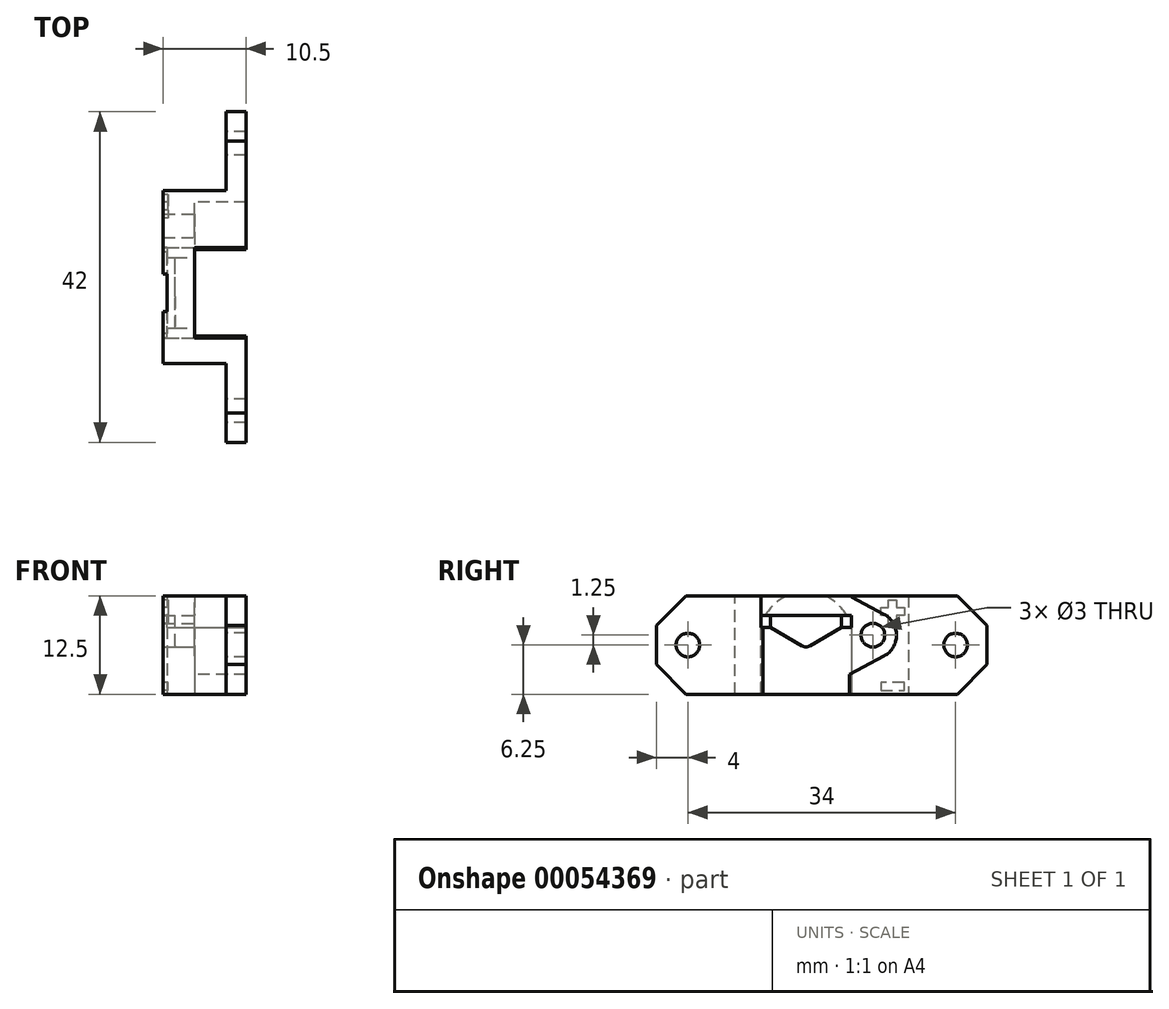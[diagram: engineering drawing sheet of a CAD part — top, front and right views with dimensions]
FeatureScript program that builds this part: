
annotation { "Feature Type Name" : "Feature", "Feature Type Description" : "" }
export const myFeature = defineFeature(function(context is Context, id is Id, definition is map)
    precondition{}
    {
        {
            var Q0;
            Q0=qCreatedBy(makeId("Right.planeOp"),FACE);
            var sketch = newSketch(context, id + "F0", { "sketchPlane" : qUnion([Q0])});
            skLineSegment(sketch, "E0", {"start": v(-5.75, 10) * mm, "end": v(-5.75, 8.5) * mm});
            skLineSegment(sketch, "E1", {"start": v(-5.75, 8.5) * mm, "end": v(-4.5, 8.5) * mm});
            skLineSegment(sketch, "E2", {"start": v(-4.5, 8.5) * mm, "end": v(-4.5, 10) * mm});
            skLineSegment(sketch, "E3", {"start": v(-4.5, 10) * mm, "end": v(-5.75, 10) * mm});
            skLineSegment(sketch, "E4.MirrorCS", {"start": v(4.5, 8.5) * mm, "end": v(4.5, 10) * mm});
            skLineSegment(sketch, "E5.MirrorCS", {"start": v(5.75, 8.5) * mm, "end": v(4.5, 8.5) * mm});
            skLineSegment(sketch, "E6.MirrorCS", {"start": v(4.5, 10) * mm, "end": v(5.75, 10) * mm});
            skLineSegment(sketch, "E7.MirrorCS", {"start": v(5.75, 10) * mm, "end": v(5.75, 8.5) * mm});
            skArc(sketch, "E8", {"start": v(-5.2, 10) * mm, "mid": v(0, 13) * mm, "end": v(5.2, 10) * mm});
            skLineSegment(sketch, "E9", {"start": v(-5.75, 8.5) * mm, "end": v(-5.75, 0) * mm});
            skLineSegment(sketch, "E10.MirrorCS", {"start": v(5.75, 8.5) * mm, "end": v(5.75, 0) * mm});
            skLineSegment(sketch, "E11", {"start": v(-5.75, 0) * mm, "end": v(5.75, 0) * mm});
            skCircle(sketch, "E12", {"center": v(0, 7) * mm, "radius": 8 * mm, "construction": true});
            skSolve(sketch);
        }
        {
            var Q0;
            Q0=qCreatedBy(makeId("Right.planeOp"),FACE);
            cPlane(context, id + "F1", {"entities" : qUnion([Q0]), "cplaneType" : CPlaneType.OFFSET, "offset" : 4 * mm, "width" : 150 * mm, "height" : 150 * mm});
        }
        {
            var Q0;
            Q0=qCreatedBy(id+"F1.planeOp",FACE);
            var sketch = newSketch(context, id + "F2", { "sketchPlane" : qUnion([Q0])});
            skLineSegment(sketch, "E13", {"start": v(-5.5, 0) * mm, "end": v(-5.5, 12.5) * mm, "construction": true});
            skLineSegment(sketch, "E14.MirrorCS", {"start": v(5.5, 0) * mm, "end": v(5.5, 12.5) * mm, "construction": true});
            skLineSegment(sketch, "E15", {"start": v(5.5, 12.5) * mm, "end": v(-5.5, 12.5) * mm, "construction": true});
            skCircle(sketch, "E16", {"center": v(8.5, 7.5) * mm, "radius": 1.5 * mm, "construction": true});
            skArc(sketch, "E17", {"start": v(9.91, 10.15) * mm, "mid": v(11.5, 7.5) * mm, "end": v(9.91, 4.85) * mm});
            skLineSegment(sketch, "E18", {"start": v(9.91, 10.15) * mm, "end": v(5.5, 12.5) * mm});
            skLineSegment(sketch, "E19", {"start": v(9.91, 4.85) * mm, "end": v(5.5, 2.5) * mm});
            skSolve(sketch);
        }
        {
            var Q0;
            Q0=qCreatedBy(id+"F1.planeOp",FACE);
            var sketch = newSketch(context, id + "F3", { "sketchPlane" : qUnion([Q0])});
            skLineSegment(sketch, "E20", {"start": v(13, 0) * mm, "end": v(13, 12.5) * mm});
            skLineSegment(sketch, "E21", {"start": v(13, 12.5) * mm, "end": v(19.25, 12.5) * mm});
            skLineSegment(sketch, "E22", {"start": v(19.25, 12.5) * mm, "end": v(23, 8.75) * mm});
            skLineSegment(sketch, "E23", {"start": v(23, 8.75) * mm, "end": v(23, 3.75) * mm});
            skLineSegment(sketch, "E24", {"start": v(23, 3.75) * mm, "end": v(19.25, 0) * mm});
            skLineSegment(sketch, "E25", {"start": v(19.25, 0) * mm, "end": v(13, 0) * mm});
            skCircle(sketch, "E26", {"center": v(19, 6.25) * mm, "radius": 1.5 * mm});
            skPoint(sketch, "E26.centerSnap0", {"position": v(13, 6.25) * mm});
            skLineSegment(sketch, "E27", {"start": v(13, 6.25) * mm, "end": v(-9, 6.25) * mm, "construction": true});
            skLineSegment(sketch, "E28", {"start": v(2, 6.25) * mm, "end": v(2, 0) * mm, "construction": true});
            skLineSegment(sketch, "E29.MirrorCS", {"start": v(-9, 0) * mm, "end": v(-9, 12.5) * mm});
            skLineSegment(sketch, "E30.MirrorCS", {"start": v(-15.25, 0) * mm, "end": v(-9, 0) * mm});
            skLineSegment(sketch, "E31.MirrorCS", {"start": v(-19, 3.75) * mm, "end": v(-15.25, 0) * mm});
            skCircle(sketch, "E32.MirrorC", {"center": v(-15, 6.25) * mm, "radius": 1.5 * mm});
            skLineSegment(sketch, "E33.MirrorCS", {"start": v(-19, 8.75) * mm, "end": v(-19, 3.75) * mm});
            skLineSegment(sketch, "E34.MirrorCS", {"start": v(-15.25, 12.5) * mm, "end": v(-19, 8.75) * mm});
            skLineSegment(sketch, "E35.MirrorCS", {"start": v(-9, 12.5) * mm, "end": v(-15.25, 12.5) * mm});
            skLineSegment(sketch, "E36", {"start": v(13, 12.5) * mm, "end": v(-9, 12.5) * mm});
            skLineSegment(sketch, "E37", {"start": v(-9, 0) * mm, "end": v(13, 0) * mm});
            skLineSegment(sketch, "E38.0", {"start": v(9.91, 4.85) * mm, "end": v(5.5, 2.5) * mm});
            skArc(sketch, "E39.0", {"start": v(9.91, 10.15) * mm, "mid": v(11.5, 7.5) * mm, "end": v(9.91, 4.85) * mm});
            skLineSegment(sketch, "E40.0", {"start": v(9.91, 10.15) * mm, "end": v(5.5, 12.5) * mm});
            skLineSegment(sketch, "E41", {"start": v(5.5, 2.5) * mm, "end": v(5.5, 0) * mm});
            skLineSegment(sketch, "E42", {"start": v(-5.5, 12.5) * mm, "end": v(-5.5, 0) * mm});
            skSolve(sketch);
        }
        {
            var Q0;
            Q0=makeQuery(id+"F3.imprint","IMPRINT",FACE,{"disambiguationData":[TD([[makeQuery(id+"F3.imprint","IMPRINT",EDGE,{"derivedFrom":sQuery(id+"F3.wireOp",EDGE,"E29.MirrorCS")}),1.0]])]});
            var Q1;
            {var subQ0=sQuery(id+"F3.wireOp",EDGE,"E29.MirrorCS");Q1=makeQuery(id+"F3.imprint","IMPRINT",FACE,{"disambiguationData":[TD([[makeQuery(id+"F3.imprint","IMPRINT",EDGE,{"derivedFrom":subQ0}),-1.0]])]});}
            var Q2;
            {var subQ0=sQuery(id+"F3.wireOp",EDGE,"E20");Q2=makeQuery(id+"F3.imprint","IMPRINT",FACE,{"disambiguationData":[TD([[makeQuery(id+"F3.imprint","IMPRINT",EDGE,{"derivedFrom":subQ0}),1.0]])]});}
            var Q3;
            Q3=makeQuery(id+"F3.imprint","IMPRINT",FACE,{"disambiguationData":[TD([[makeQuery(id+"F3.imprint","IMPRINT",EDGE,{"derivedFrom":sQuery(id+"F3.wireOp",EDGE,"E20")}),-1.0]])]});
            extrude(context, id + "F4", {"entities" : qUnion([Q0, Q1, Q2, Q3]), "depth" : 6.5 * mm});
        }
        {
            var Q0;
            Q0=qCreatedBy(id+"F1.planeOp",FACE);
            var sketch = newSketch(context, id + "F5", { "sketchPlane" : qUnion([Q0])});
            skLineSegment(sketch, "E43", {"start": v(-5.75, 12.5) * mm, "end": v(-5.75, 8.5) * mm});
            skLineSegment(sketch, "E44", {"start": v(-5.75, 8.5) * mm, "end": v(-4.5, 8.5) * mm});
            skLineSegment(sketch, "E45", {"start": v(5.75, 8.5) * mm, "end": v(5.75, 12.5) * mm});
            skLineSegment(sketch, "E46.0", {"start": v(-4.5, 10) * mm, "end": v(-5.75, 10) * mm});
            skLineSegment(sketch, "E47.0", {"start": v(-4.5, 8.5) * mm, "end": v(-4.5, 10) * mm});
            skLineSegment(sketch, "E48.0", {"start": v(4.5, 10) * mm, "end": v(5.75, 10) * mm});
            skLineSegment(sketch, "E49.0", {"start": v(4.5, 8.5) * mm, "end": v(4.5, 10) * mm});
            skLineSegment(sketch, "E50", {"start": v(-5.75, 12.5) * mm, "end": v(-9, 12.5) * mm});
            skLineSegment(sketch, "E51", {"start": v(-9, 12.5) * mm, "end": v(-9, 0) * mm});
            skLineSegment(sketch, "E52", {"start": v(-9, 0) * mm, "end": v(13, 0) * mm});
            skLineSegment(sketch, "E53", {"start": v(13, 0) * mm, "end": v(13, 12.5) * mm});
            skLineSegment(sketch, "E54", {"start": v(13, 12.5) * mm, "end": v(5.75, 12.5) * mm});
            skLineSegment(sketch, "E55", {"start": v(-5.75, 12.5) * mm, "end": v(5.75, 12.5) * mm});
            skCircle(sketch, "E56.0", {"center": v(8.5, 7.5) * mm, "radius": 1.5 * mm});
            skArc(sketch, "E57", {"start": v(-0.5, 6.14) * mm, "mid": v(0, 6) * mm, "end": v(0.5, 6.14) * mm});
            skLineSegment(sketch, "E58", {"start": v(0.5, 6.14) * mm, "end": v(4.5, 8.5) * mm});
            skLineSegment(sketch, "E59", {"start": v(-0.5, 6.14) * mm, "end": v(-4.5, 8.5) * mm});
            skLineSegment(sketch, "E60.trimOffspring", {"start": v(4.5, 8.5) * mm, "end": v(5.75, 8.5) * mm});
            skLineSegment(sketch, "E61", {"start": v(-4.5, 10) * mm, "end": v(4.5, 10) * mm});
            skSolve(sketch);
        }
        {
            var Q0;
            {var subQ5=sQuery(id+"F5.wireOp",EDGE,"E50");Q0=makeQuery(id+"F5.imprint","IMPRINT",FACE,{"disambiguationData":[TD([[makeQuery(id+"F5.imprint","IMPRINT",EDGE,{"derivedFrom":subQ5}),1.0]])]});}
            var Q1;
            {var subQ0=sQuery(id+"F5.wireOp",EDGE,"E46.0");Q1=makeQuery(id+"F5.imprint","IMPRINT",FACE,{"disambiguationData":[TD([[makeQuery(id+"F5.imprint","IMPRINT",EDGE,{"derivedFrom":subQ0}),-1.0]])]});}
            var Q2;
            Q2=makeQuery(id+"F5.imprint","IMPRINT",FACE,{"disambiguationData":[TD([[makeQuery(id+"F5.imprint","IMPRINT",EDGE,{"derivedFrom":sQuery(id+"F5.wireOp",EDGE,"E47.0")}),-1.0]])]});
            var Q3;
            Q3=qCreatedBy(makeId("Right.planeOp"),FACE);
            extrude(context, id + "F6", {"entities" : qUnion([Q0, Q1, Q2]), "operationType" : NewBodyOperationType.ADD, "endBound" : BoundingType.UP_TO_SURFACE, "oppositeDirection" : true, "endBoundEntityFace" : qUnion([Q3]), "depth" : 25 * mm});
        }
        {
            var Q0;
            Q0=makeQuery(id+"F5.imprint","IMPRINT",FACE,{"disambiguationData":[TD([[makeQuery(id+"F5.imprint","IMPRINT",EDGE,{"derivedFrom":sQuery(id+"F5.wireOp",EDGE,"E47.0")}),-1.0]])]});
            extrude(context, id + "F7", {"entities" : qUnion([Q0]), "operationType" : NewBodyOperationType.REMOVE, "oppositeDirection" : true, "depth" : 2.5 * mm});
        }
        {
            var Q0;
            Q0=makeQuery(id+"F3.imprint","IMPRINT",FACE,{"disambiguationData":[TD([[makeQuery(id+"F3.imprint","IMPRINT",EDGE,{"derivedFrom":sQuery(id+"F3.wireOp",EDGE,"E29.MirrorCS")}),1.0]])]});
            var Q1;
            Q1=makeQuery(id+"F3.imprint","IMPRINT",FACE,{"disambiguationData":[TD([[makeQuery(id+"F3.imprint","IMPRINT",EDGE,{"derivedFrom":sQuery(id+"F3.wireOp",EDGE,"E20")}),-1.0]])]});
            extrude(context, id + "F8", {"entities" : qUnion([Q0, Q1]), "operationType" : NewBodyOperationType.REMOVE, "depth" : 4 * mm});
        }
        {
            var Q0;
            {var subQ0=sQuery(id+"F5.wireOp",EDGE,"E46.0");Q0=makeQuery(id+"F5.imprint","IMPRINT",FACE,{"disambiguationData":[TD([[makeQuery(id+"F5.imprint","IMPRINT",EDGE,{"derivedFrom":subQ0}),-1.0]])]});}
            var Q1;
            {var subQ3=sQuery(id+"F5.wireOp",EDGE,"E46.0");Q1=makeQuery(id+"F5.imprint","IMPRINT",FACE,{"disambiguationData":[TD([[makeQuery(id+"F5.imprint","IMPRINT",EDGE,{"derivedFrom":subQ3}),1.0]])]});}
            extrude(context, id + "F9", {"entities" : qUnion([Q0, Q1]), "operationType" : NewBodyOperationType.REMOVE, "depth" : 25 * mm});
        }
        {
            var Q0;
            Q0=makeQuery(id+"F6.opExtrude","CAP_FACE",FACE,{"disambiguationData":[OSD([sQuery(id+"F5.wireOp",EDGE,"E43"),sQuery(id+"F5.wireOp",EDGE,"E44"),sQuery(id+"F5.wireOp",EDGE,"E45"),sQuery(id+"F5.wireOp",EDGE,"E46.0"),sQuery(id+"F5.wireOp",EDGE,"E47.0"),sQuery(id+"F5.wireOp",EDGE,"E48.0"),sQuery(id+"F5.wireOp",EDGE,"E49.0"),sQuery(id+"F5.wireOp",EDGE,"E50"),sQuery(id+"F5.wireOp",EDGE,"E51"),sQuery(id+"F5.wireOp",EDGE,"E52"),sQuery(id+"F5.wireOp",EDGE,"E53"),sQuery(id+"F5.wireOp",EDGE,"E54"),sQuery(id+"F5.wireOp",EDGE,"E55"),sQuery(id+"F5.wireOp",EDGE,"E56.0"),sQuery(id+"F5.wireOp",EDGE,"E60.trimOffspring")])],"isStart":false});
            var sketch = newSketch(context, id + "F10", { "sketchPlane" : qUnion([Q0])});
            skLineSegment(sketch, "E62", {"start": v(-11.5, 12) * mm, "end": v(-11.5, 11) * mm});
            skLineSegment(sketch, "E63", {"start": v(-11.5, 11) * mm, "end": v(-12.5, 11) * mm});
            skLineSegment(sketch, "E64", {"start": v(-12.5, 11) * mm, "end": v(-12.5, 10) * mm});
            skLineSegment(sketch, "E65", {"start": v(-12.5, 10) * mm, "end": v(-11.5, 10) * mm});
            skLineSegment(sketch, "E66", {"start": v(-11.5, 10) * mm, "end": v(-11.5, 9) * mm});
            skLineSegment(sketch, "E67", {"start": v(-11.5, 9) * mm, "end": v(-10.5, 9) * mm});
            skLineSegment(sketch, "E68", {"start": v(-10.5, 9) * mm, "end": v(-10.5, 10) * mm});
            skLineSegment(sketch, "E69", {"start": v(-10.5, 10) * mm, "end": v(-9.5, 10) * mm});
            skLineSegment(sketch, "E70", {"start": v(-9.5, 10) * mm, "end": v(-9.5, 11) * mm});
            skLineSegment(sketch, "E71", {"start": v(-9.5, 11) * mm, "end": v(-10.5, 11) * mm});
            skLineSegment(sketch, "E72", {"start": v(-10.5, 11) * mm, "end": v(-10.5, 12) * mm});
            skLineSegment(sketch, "E73", {"start": v(-10.5, 12) * mm, "end": v(-11.5, 12) * mm});
            skLineSegment(sketch, "E74", {"start": v(-12.5, 1.5) * mm, "end": v(-9.5, 1.5) * mm});
            skLineSegment(sketch, "E75", {"start": v(-9.5, 1.5) * mm, "end": v(-9.5, 0.5) * mm});
            skLineSegment(sketch, "E76", {"start": v(-9.5, 0.5) * mm, "end": v(-12.5, 0.5) * mm});
            skLineSegment(sketch, "E77", {"start": v(-12.5, 0.5) * mm, "end": v(-12.5, 1.5) * mm});
            skSolve(sketch);
        }
        {
            var Q0;
            Q0=makeQuery(id+"F10.imprint","IMPRINT",FACE,{"disambiguationData":[TD([[makeQuery(id+"F10.imprint","IMPRINT",EDGE,{"derivedFrom":sQuery(id+"F10.wireOp",EDGE,"E62")}),1.0]])]});
            var Q1;
            Q1=makeQuery(id+"F10.imprint","IMPRINT",FACE,{"disambiguationData":[TD([[makeQuery(id+"F10.imprint","IMPRINT",EDGE,{"derivedFrom":sQuery(id+"F10.wireOp",EDGE,"E74")}),-1.0]])]});
            extrude(context, id + "F11", {"entities" : qUnion([Q0, Q1]), "operationType" : NewBodyOperationType.REMOVE, "oppositeDirection" : true, "depth" : 0.6 * mm});
        }
        {
            var Q0;
            Q0=makeQuery(id+"F0.imprint","IMPRINT",FACE,{"disambiguationData":[TD([[makeQuery(id+"F0.imprint","IMPRINT",EDGE,{"derivedFrom":sQuery(id+"F0.wireOp",EDGE,"E1")}),-1.0]])]});
            extrude(context, id + "F12", {"entities" : qUnion([Q0]), "operationType" : NewBodyOperationType.REMOVE, "depth" : 0.5 * mm});
        }
    });
